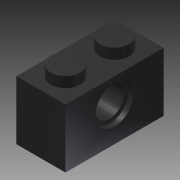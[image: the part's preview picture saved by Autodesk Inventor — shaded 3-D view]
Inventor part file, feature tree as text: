
AUTODESK INVENTOR PART (.ipt)
format: ipt  version: 2013 (Build 170138000, 138)  size: 167,936 bytes
history: native  units: mm
features: extrude x6, sketch x3, pattern_linear x2, plane x1, mirror x1
ambient origin geometry x8: Origin, YZ Plane, XZ Plane, XY Plane, X Axis, Y Axis, Z Axis, Center Point
bodies: Solid1 (feature_tree)
feature tree (13):
  sketch  "Sketch1"  dims[d0=8.0mm d1=8.0mm]
  extrude  "Extrusion1"  Depth=8.0mm
  extrude  "Extrusion2"  Depth=9.6mm TaperAngle=0.0deg
  pattern_linear  "Rectangular Pattern1"  Count1=2 Spacing1=8.0mm
  extrude  "Extrusion6"  Depth=4.8mm
  sketch  "Sketch2"  dims[d2=4.8mm d3=9.6mm d4=0.0mm]
  plane  "Work Plane1"
  extrude  "Extrusion4"  Depth=6.2mm
  extrude  "Extrusion5"  Depth=1.7mm TaperAngle=0.0deg
  mirror  "Mirror1"
  pattern_linear  "Rectangular Pattern2"  Spacing1=0.8mm  [1 undecoded]
  extrude  "Extrusion7"  Depth=10.0mm
  sketch  "Sketch3"  dims[d5=11.3mm d6=0.0mm d9=20.0mm d11=8.0mm d12=4.8mm d14=6.2mm d15=1.7mm d16=0.0mm d17=0.8mm d18=0.0mm d19=10.0mm d21=8.0mm d22=1.6mm d23=3.2mm d24=8.0mm d25=8.0mm d26=0.0mm d27=8.0mm d28=0.0mm d29=8.0mm d30=8.0mm d31=5.6mm]
note: 1 required parameter value undecoded (feature->parameter linkage not recoverable at this tier; creation-order binding heuristic only, values carry confidence <= 0.55)
